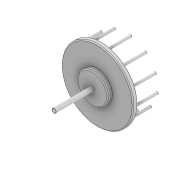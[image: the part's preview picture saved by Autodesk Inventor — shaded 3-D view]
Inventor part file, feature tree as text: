
AUTODESK INVENTOR PART (.ipt)
format: ipt  version: 2021 (Build 250183000, 183)  size: 181,760 bytes
history: native  units: in
note: dims shown in document units (in); Inventor stores cm internally (conversion verified against a paired STEP export)
features: sketch x11, extrude x7, fillet x3, projected_geometry x1
ambient origin geometry x8: Origin, YZ Plane, XZ Plane, XY Plane, X Axis, Y Axis, Z Axis, Center Point
bodies: Solid1 (feature_tree)
feature tree (22):
  extrude  "Extrusion1"  Depth=0.3937in TaperAngle=0.0deg
  fillet  "Fillet1"  Radius=0.0787in
  fillet  "Fillet2"  Radius=0.0787in
  sketch  "Sketch24"  dims[d104=0.1969in d105=4.7244in d107=360.0deg]
  sketch  "Sketch25"  dims[d109=1.9685in d110=0.0in d111=0.1969in]
  sketch  "Sketch26"  dims[d112=1.9685in d113=0.0in d114=0.315in]
  extrude  "Extrusion6"  Depth=4.7244in TaperAngle=360.0deg
  extrude  "Extrusion7"  Depth=1.9685in
  sketch  "Sketch30"  dims[d120=0.3543in d121=3.1496in d122=0.0in]
  sketch  "Sketch31"  dims[d123=0.315in d124=0.3937in d125=0.0in]
  extrude  "Extrusion8"  Depth=0.315in
  extrude  "Extrusion9"  Depth=0.3937in TaperAngle=0.0deg
  fillet  "Fillet3"  Radius=0.0787in
  extrude  "Extrusion10"  Depth=3.1496in TaperAngle=0.0deg
  extrude  "Extrusion11"  Depth=0.3937in TaperAngle=0.0deg
  sketch  "Sketch2"  dims[d0=5.9055in d1=0.3937in d2=0.0in d59=0.0787in d60=0.0787in]
  projected_geometry  "Projected Loop2"
  sketch  "Sketch29"  dims[d115=0.3937in d116=0.0in d117=0.3937in d118=0.0in d119=0.0787in]
  sketch  "Sketch32"  dims[d12=0.0394in]
  sketch  "Sketch33"  dims[d13=0.0394in]
  sketch  "Sketch34"  dims[d14=0.0394in]
  sketch  "Sketch35"  dims[d15=0.0059in d16=0.0098in d17=0.0148in d18=0.5635in d19=0.0295in d20=0.8108in d21=0.0025in d22=0.0295in d23=0.0148in d43=0.0394in d44=0.0394in d45=0.0394in d46=0.0059in d47=0.0098in d48=0.0148in d49=0.5635in d50=0.0295in d51=0.8108in d52=0.0025in d53=0.0295in d54=0.0148in d126=0.0197in d127=0.0344in]
